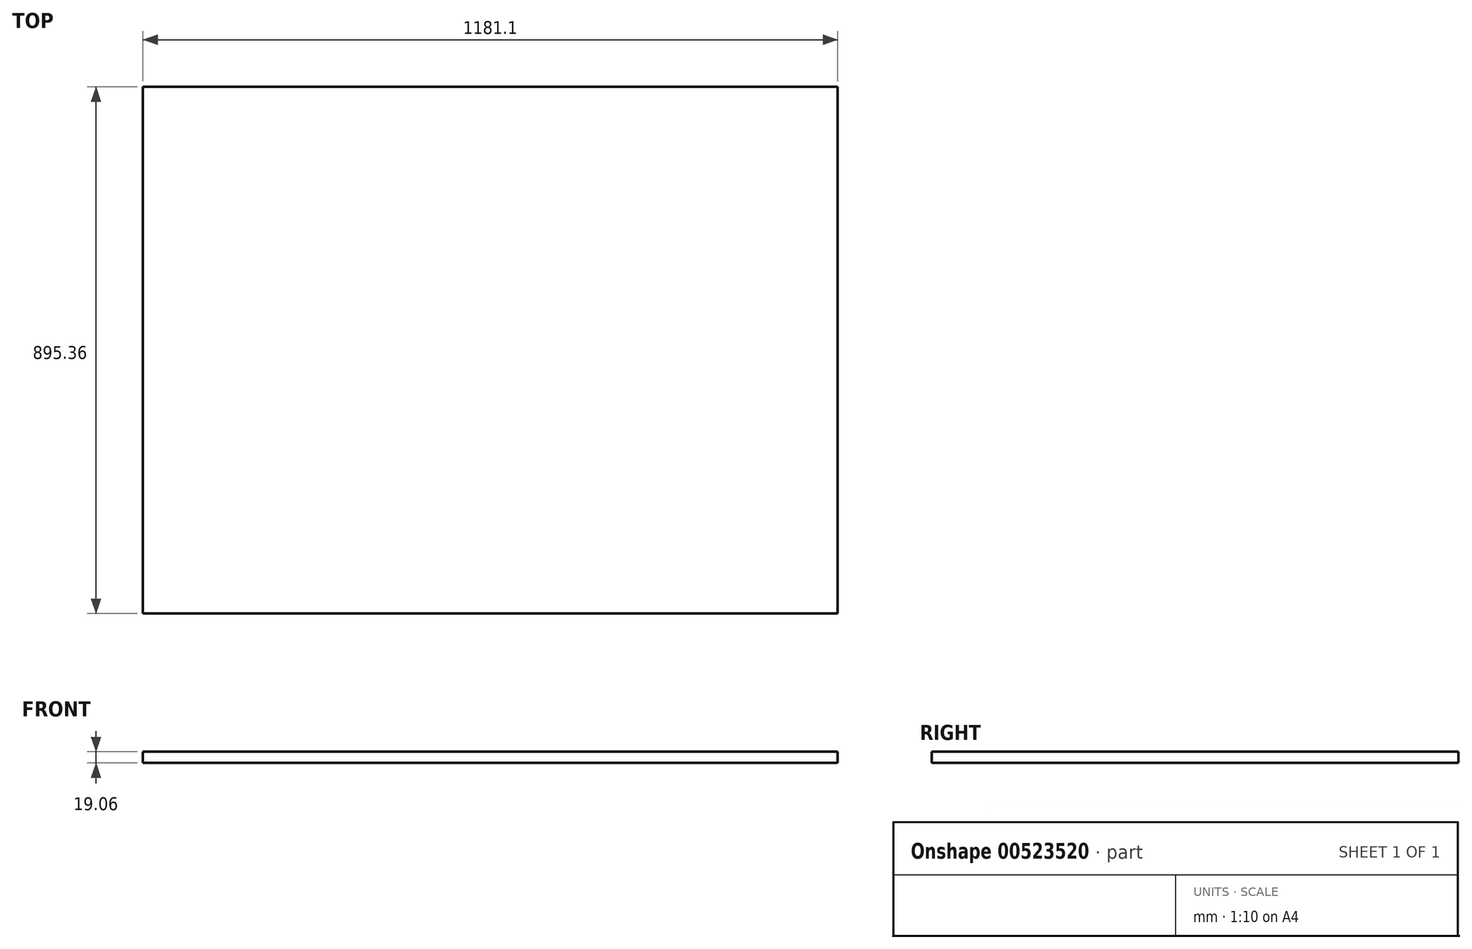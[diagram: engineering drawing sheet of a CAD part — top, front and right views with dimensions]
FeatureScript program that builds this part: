
annotation { "Feature Type Name" : "Feature", "Feature Type Description" : "" }
export const myFeature = defineFeature(function(context is Context, id is Id, definition is map)
    precondition{}
    {
        {
            var Q0;
            Q0=qCreatedBy(makeId("Top.planeOp"),FACE);
            var sketch = newSketch(context, id + "F0", { "sketchPlane" : qUnion([Q0])});
            skLineSegment(sketch, "E0.bottom", {"start": v(-590.55, 447.68) * mm, "end": v(590.55, 447.68) * mm});
            skLineSegment(sketch, "E0.top", {"start": v(-590.55, -447.68) * mm, "end": v(590.55, -447.68) * mm});
            skLineSegment(sketch, "E0.left", {"start": v(-590.55, 447.68) * mm, "end": v(-590.55, -447.68) * mm});
            skLineSegment(sketch, "E0.right", {"start": v(590.55, 447.68) * mm, "end": v(590.55, -447.68) * mm});
            skPoint(sketch, "E0.middle", {"position": v(0, 0) * mm});
            skSolve(sketch);
        }
        {
            var Q0;
            Q0=makeQuery(id+"F0.imprint","IMPRINT",FACE,{"disambiguationData":[TD([[makeQuery(id+"F0.imprint","IMPRINT",EDGE,{"derivedFrom":sQuery(id+"F0.wireOp",EDGE,"E0.bottom")}),-1.0]])]});
            extrude(context, id + "F1", {"entities" : qUnion([Q0]), "endBound" : BoundingType.SYMMETRIC, "depth" : 19.05 * mm, "offsetDistance" : 25.4 * mm});
        }
    });
